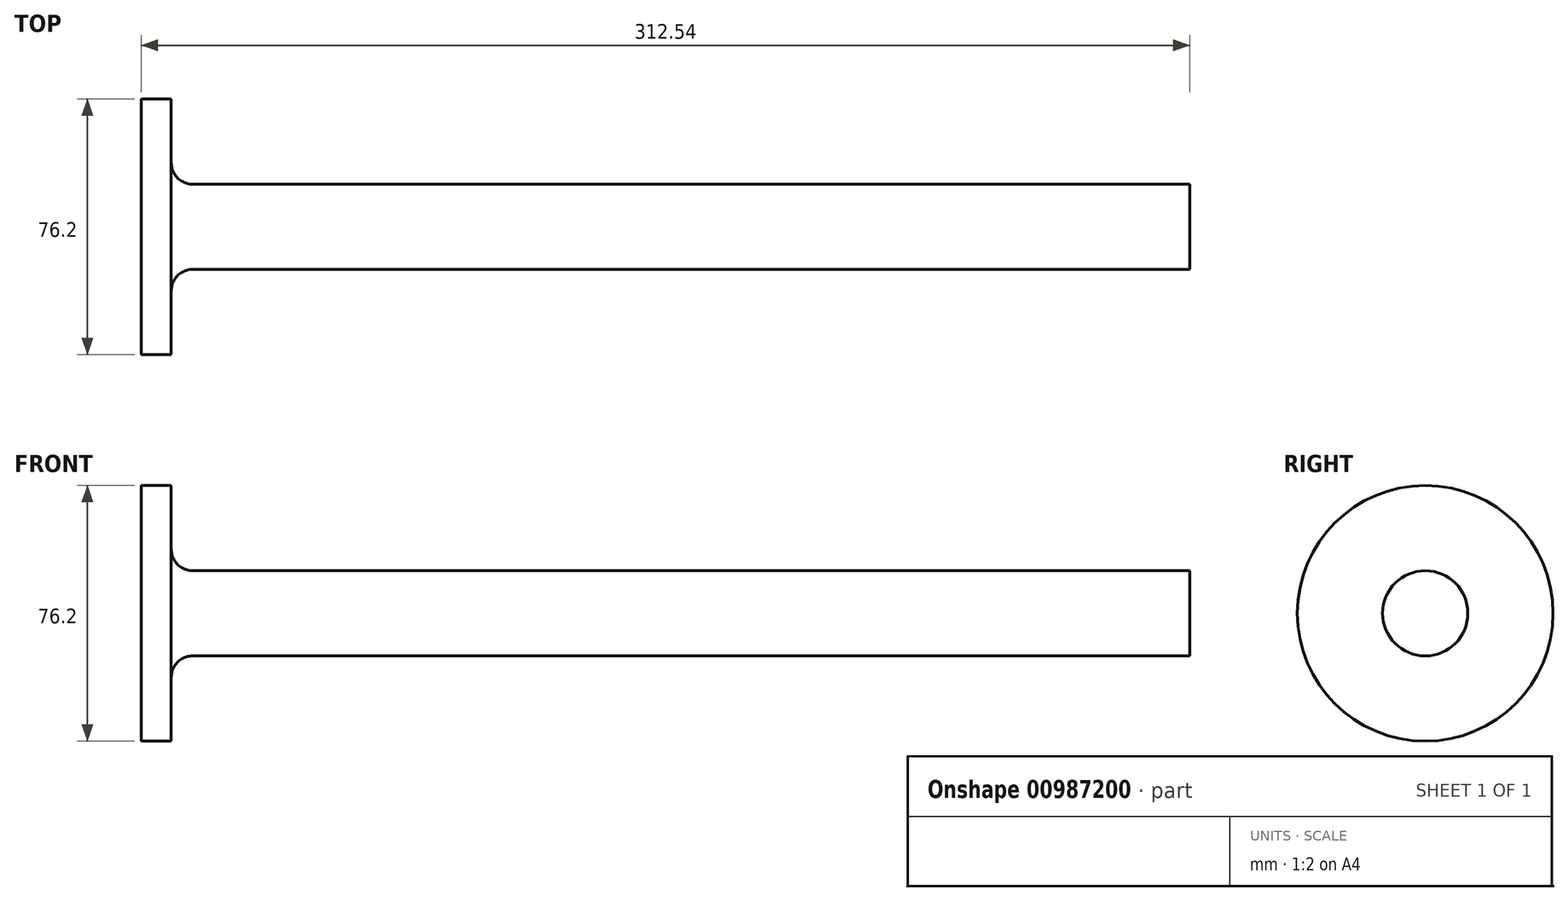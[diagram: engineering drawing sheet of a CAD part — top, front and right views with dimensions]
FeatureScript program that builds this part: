
annotation { "Feature Type Name" : "Feature", "Feature Type Description" : "" }
export const myFeature = defineFeature(function(context is Context, id is Id, definition is map)
    precondition{}
    {
        {
            var Q0;
            Q0=qCreatedBy(makeId("Front.planeOp"),FACE);
            var sketch = newSketch(context, id + "F0", { "sketchPlane" : qUnion([Q0])});
            skLineSegment(sketch, "E0", {"start": v(0, 0) * mm, "end": v(-624.48, 0) * mm});
            skLineSegment(sketch, "E1.left", {"start": v(-312.54, 12.7) * mm, "end": v(-312.54, -12.7) * mm});
            skLineSegment(sketch, "E2.bottom", {"start": v(-312.54, 38.1) * mm, "end": v(-303.53, 38.1) * mm});
            skLineSegment(sketch, "E2.top", {"start": v(-312.54, -38.1) * mm, "end": v(-303.53, -38.1) * mm});
            skLineSegment(sketch, "E2.left", {"start": v(-312.54, 38.1) * mm, "end": v(-312.54, -38.1) * mm});
            skLineSegment(sketch, "E2.right", {"start": v(-303.53, 38.1) * mm, "end": v(-303.53, 19.05) * mm});
            skLineSegment(sketch, "E3.trimOffspring", {"start": v(-303.53, -19.05) * mm, "end": v(-303.53, -38.1) * mm});
            skPoint(sketch, "E4.visualSharp", {"position": v(-303.53, -12.7) * mm});
            skArc(sketch, "E4.filletArc", {"start": v(-297.18, -12.7) * mm, "mid": v(-301.67, -14.56) * mm, "end": v(-303.53, -19.05) * mm});
            skPoint(sketch, "E5.visualSharp", {"position": v(-303.53, 12.7) * mm});
            skArc(sketch, "E5.filletArc", {"start": v(-303.53, 19.05) * mm, "mid": v(-301.67, 14.56) * mm, "end": v(-297.18, 12.7) * mm});
            skLineSegment(sketch, "E6", {"start": v(0, 12.7) * mm, "end": v(0, -12.7) * mm});
            skLineSegment(sketch, "E7", {"start": v(0, -12.7) * mm, "end": v(-297.18, -12.7) * mm});
            skArc(sketch, "E8.MirrorCS", {"start": v(297.18, -12.7) * mm, "mid": v(301.67, -14.56) * mm, "end": v(303.53, -19.05) * mm});
            skLineSegment(sketch, "E9.MirrorCS", {"start": v(312.54, -38.1) * mm, "end": v(303.53, -38.1) * mm});
            skLineSegment(sketch, "E10.MirrorCS", {"start": v(312.54, 12.7) * mm, "end": v(312.54, -12.7) * mm});
            skLineSegment(sketch, "E11.MirrorCS", {"start": v(303.53, -19.05) * mm, "end": v(303.53, -38.1) * mm});
            skPoint(sketch, "E12.MirrorP", {"position": v(303.53, -12.7) * mm});
            skLineSegment(sketch, "E13.MirrorCS", {"start": v(0, -12.7) * mm, "end": v(297.18, -12.7) * mm});
            skLineSegment(sketch, "E14.MirrorCS", {"start": v(312.54, 38.1) * mm, "end": v(312.54, -38.1) * mm});
            skLineSegment(sketch, "E15", {"start": v(0, 0) * mm, "end": v(327.88, 0) * mm});
            skSolve(sketch);
        }
        {
            var Q0;
            {var subQ1=sQuery(id+"F0.wireOp",EDGE,"E2.top");Q0=makeQuery(id+"F0.imprint","IMPRINT",FACE,{"disambiguationData":[TD([[makeQuery(id+"F0.imprint","IMPRINT",EDGE,{"derivedFrom":subQ1}),1.0]])]});}
            var Q1;
            Q1=makeQuery(id+"F0.imprint","IMPRINT",FACE,{"disambiguationData":[TD([[makeQuery(id+"F0.imprint","IMPRINT",EDGE,{"derivedFrom":sQuery(id+"F0.wireOp",EDGE,"E8.MirrorCS")}),1.0]])]});
            var Q2;
            Q2=sQuery(id+"F0.wireOp",EDGE,"E0");
            revolve(context, id + "F1", {"surfaceOperationType" : NewSurfaceOperationType.NEW, "entities" : qUnion([Q0, Q1]), "axis" : qUnion([Q2]), "revolveType" : RevolveType.FULL});
        }
    });
